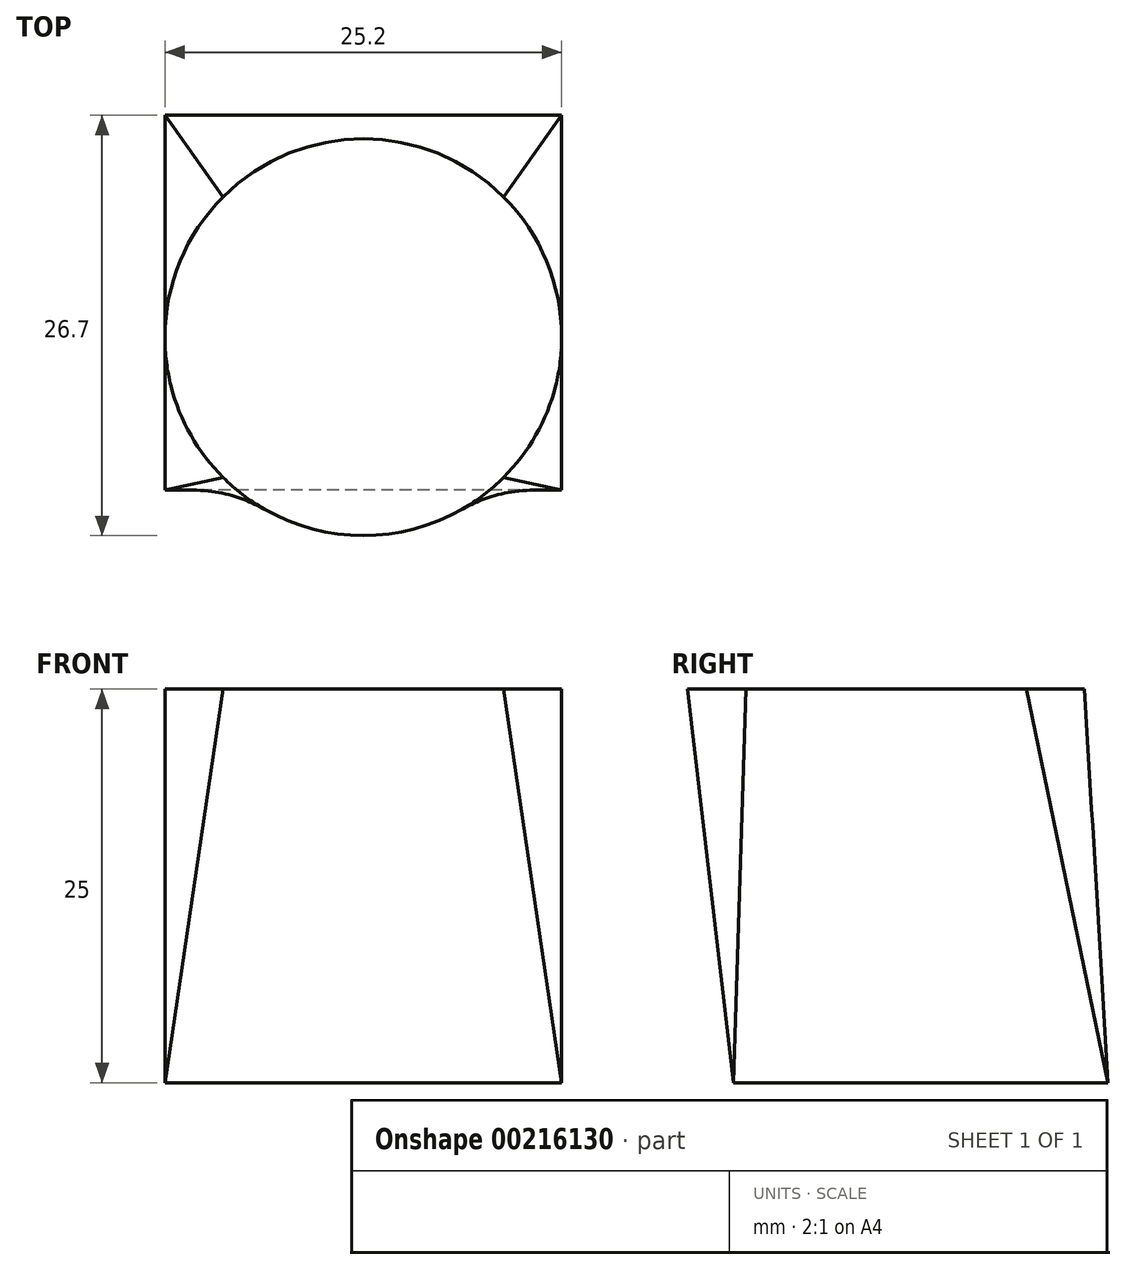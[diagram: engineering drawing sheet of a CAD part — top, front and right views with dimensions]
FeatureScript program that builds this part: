
annotation { "Feature Type Name" : "Feature", "Feature Type Description" : "" }
export const myFeature = defineFeature(function(context is Context, id is Id, definition is map)
    precondition{}
    {
        {
            var Q0;
            Q0=qCreatedBy(makeId("Top.planeOp"),FACE);
            var sketch = newSketch(context, id + "F0", { "sketchPlane" : qUnion([Q0])});
            skLineSegment(sketch, "E0.bottom", {"start": v(12.6, 11.9) * mm, "end": v(-12.6, 11.9) * mm});
            skLineSegment(sketch, "E0.top", {"start": v(12.6, -11.9) * mm, "end": v(-12.6, -11.9) * mm});
            skLineSegment(sketch, "E0.left", {"start": v(12.6, 11.9) * mm, "end": v(12.6, -11.9) * mm});
            skLineSegment(sketch, "E0.right", {"start": v(-12.6, 11.9) * mm, "end": v(-12.6, -11.9) * mm});
            skPoint(sketch, "E0.middle", {"position": v(0, 0) * mm});
            skLineSegment(sketch, "E1", {"start": v(0, 22.76) * mm, "end": v(0, -19.74) * mm, "construction": true});
            skLineSegment(sketch, "E2", {"start": v(-28.28, -2.2) * mm, "end": v(26.23, -2.2) * mm, "construction": true});
            skPoint(sketch, "E3", {"position": v(0, -2.2) * mm});
            skSolve(sketch);
        }
        {
            var Q0;
            Q0=makeQuery(id+"F0.imprint","IMPRINT",FACE,{"disambiguationData":[TD([[makeQuery(id+"F0.imprint","IMPRINT",EDGE,{"derivedFrom":sQuery(id+"F0.wireOp",EDGE,"E0.bottom")}),1.0]])]});
            cPlane(context, id + "F1", {"entities" : qUnion([Q0]), "cplaneType" : CPlaneType.OFFSET, "offset" : 25 * mm, "width" : 150 * mm, "height" : 150 * mm});
        }
        {
            var Q0;
            Q0=qCreatedBy(id+"F1.planeOp",FACE);
            var sketch = newSketch(context, id + "F2", { "sketchPlane" : qUnion([Q0])});
            skLineSegment(sketch, "E4", {"start": v(-19.06, -2.2) * mm, "end": v(19.4, -2.2) * mm, "construction": true});
            skLineSegment(sketch, "E5", {"start": v(0, 16.48) * mm, "end": v(0, -24.4) * mm, "construction": true});
            skLineSegment(sketch, "E6", {"start": v(15.09, 12.89) * mm, "end": v(0, -2.2) * mm, "construction": true});
            skLineSegment(sketch, "E7", {"start": v(0, -2.2) * mm, "end": v(-14.4, -16.6) * mm, "construction": true});
            skLineSegment(sketch, "E8", {"start": v(0, -2.2) * mm, "end": v(8.9, -11.1) * mm, "construction": true});
            skLineSegment(sketch, "E9", {"start": v(0, -2.2) * mm, "end": v(-14.13, 11.93) * mm, "construction": true});
            skLineSegment(sketch, "E10", {"start": v(-8.9, 6.7) * mm, "end": v(-8.9, 6.7) * mm});
            skArc(sketch, "E11", {"start": v(8.9, 6.7) * mm, "mid": v(0, 10.4) * mm, "end": v(-8.9, 6.7) * mm});
            skLineSegment(sketch, "E12", {"start": v(8.9, 6.7) * mm, "end": v(8.9, 6.7) * mm});
            skArc(sketch, "E13", {"start": v(8.9, -11.1) * mm, "mid": v(12.6, -2.2) * mm, "end": v(8.9, 6.7) * mm});
            skLineSegment(sketch, "E14", {"start": v(8.9, -11.1) * mm, "end": v(12.84, -15.04) * mm, "construction": true});
            skLineSegment(sketch, "E15", {"start": v(-8.9, -11.1) * mm, "end": v(-8.9, -11.1) * mm});
            skArc(sketch, "E16", {"start": v(-8.9, -11.1) * mm, "mid": v(0, -14.8) * mm, "end": v(8.9, -11.1) * mm});
            skArc(sketch, "E17", {"start": v(-8.9, 6.7) * mm, "mid": v(-12.6, -2.2) * mm, "end": v(-8.9, -11.1) * mm});
            skSolve(sketch);
        }
        {
            var Q0;
            Q0=makeQuery(id+"F2.imprint","IMPRINT",FACE,{"disambiguationData":[TD([[makeQuery(id+"F2.imprint","IMPRINT",EDGE,{"derivedFrom":sQuery(id+"F2.wireOp",EDGE,"E11")}),1.0]])]});
            var Q1;
            Q1=makeQuery(id+"F0.imprint","IMPRINT",FACE,{"disambiguationData":[TD([[makeQuery(id+"F0.imprint","IMPRINT",EDGE,{"derivedFrom":sQuery(id+"F0.wireOp",EDGE,"E0.bottom")}),1.0]])]});
            loft(context, id + "F3", {"sheetProfilesArray" : [{ "sheetProfileEntities" : qUnion([Q0]) }, { "sheetProfileEntities" : qUnion([Q1]) }]});
        }
    });
